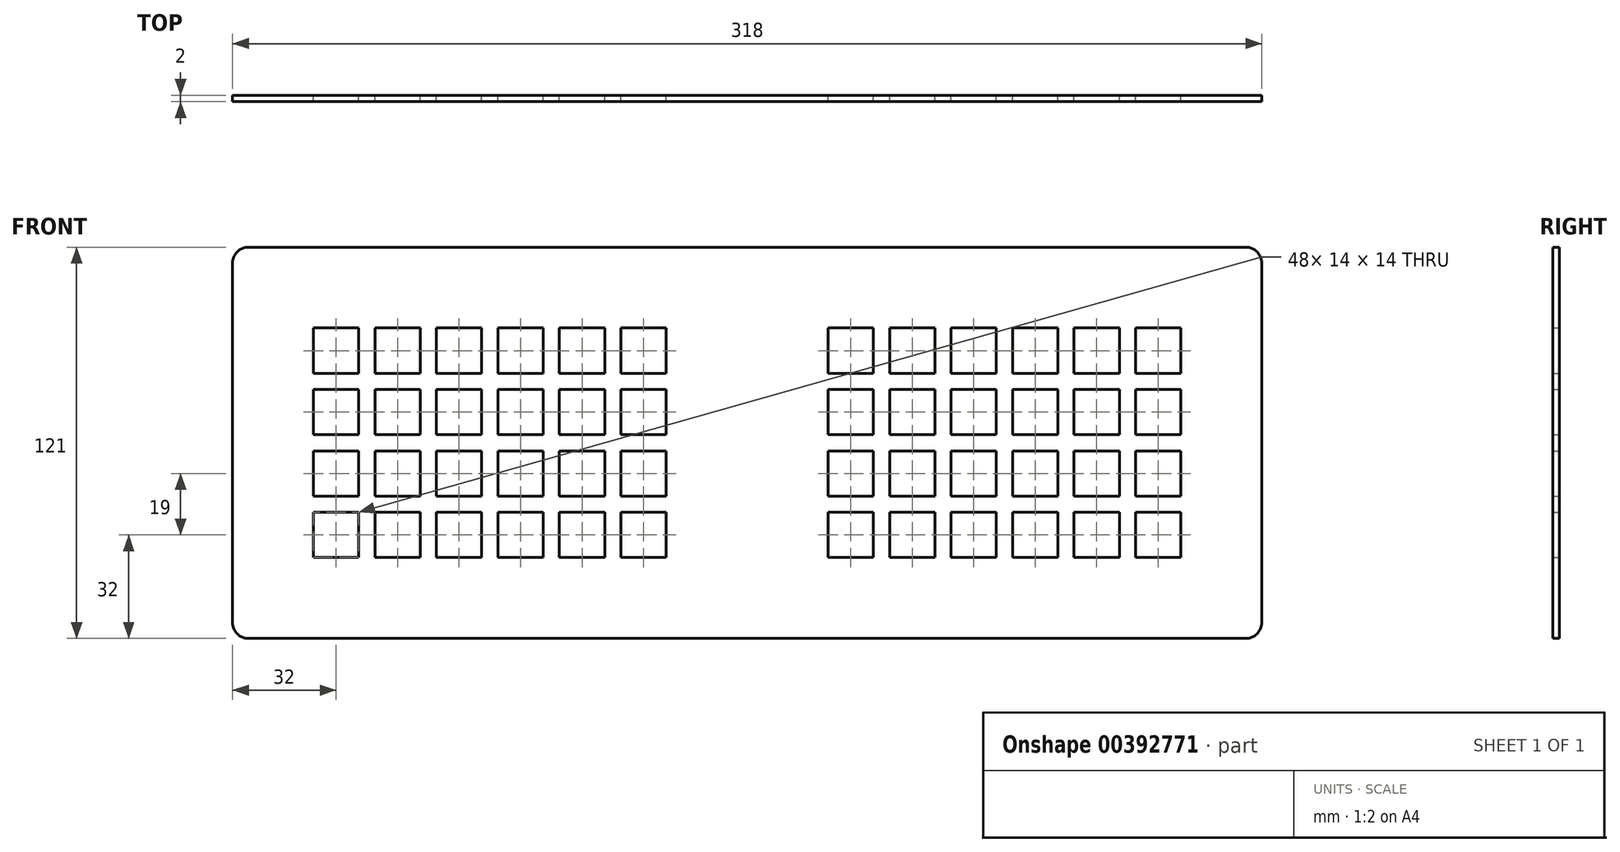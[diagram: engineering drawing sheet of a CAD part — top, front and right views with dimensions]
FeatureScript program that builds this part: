
annotation { "Feature Type Name" : "Feature", "Feature Type Description" : "" }
export const myFeature = defineFeature(function(context is Context, id is Id, definition is map)
    precondition{}
    {
        {
            var Q0;
            Q0=qCreatedBy(makeId("Front.planeOp"),FACE);
            var sketch = newSketch(context, id + "F0", { "sketchPlane" : qUnion([Q0])});
            skLineSegment(sketch, "E0.bottom", {"start": v(-120, 21.5) * mm, "end": v(-134, 21.5) * mm});
            skLineSegment(sketch, "E0.top", {"start": v(-120, 35.5) * mm, "end": v(-134, 35.5) * mm});
            skLineSegment(sketch, "E0.left", {"start": v(-120, 21.5) * mm, "end": v(-120, 35.5) * mm});
            skLineSegment(sketch, "E0.right", {"start": v(-134, 21.5) * mm, "end": v(-134, 35.5) * mm});
            skPoint(sketch, "E0.middle", {"position": v(-127, 28.5) * mm});
            skLineSegment(sketch, "E1.0.1.0", {"start": v(-120, 2.5) * mm, "end": v(-120, 16.5) * mm});
            skLineSegment(sketch, "E1.0.1.1", {"start": v(-134, 2.5) * mm, "end": v(-134, 16.5) * mm});
            skLineSegment(sketch, "E1.0.1.2", {"start": v(-120, 16.5) * mm, "end": v(-134, 16.5) * mm});
            skLineSegment(sketch, "E1.0.1.3", {"start": v(-120, 2.5) * mm, "end": v(-134, 2.5) * mm});
            skPoint(sketch, "E1.0.1.4", {"position": v(-127, 9.5) * mm});
            skLineSegment(sketch, "E1.0.2.0", {"start": v(-120, -16.5) * mm, "end": v(-120, -2.5) * mm});
            skLineSegment(sketch, "E1.0.2.1", {"start": v(-134, -16.5) * mm, "end": v(-134, -2.5) * mm});
            skLineSegment(sketch, "E1.0.2.2", {"start": v(-120, -2.5) * mm, "end": v(-134, -2.5) * mm});
            skLineSegment(sketch, "E1.0.2.3", {"start": v(-120, -16.5) * mm, "end": v(-134, -16.5) * mm});
            skPoint(sketch, "E1.0.2.4", {"position": v(-127, -9.5) * mm});
            skLineSegment(sketch, "E1.0.3.0", {"start": v(-120, -35.5) * mm, "end": v(-120, -21.5) * mm});
            skLineSegment(sketch, "E1.0.3.1", {"start": v(-134, -35.5) * mm, "end": v(-134, -21.5) * mm});
            skLineSegment(sketch, "E1.0.3.2", {"start": v(-120, -21.5) * mm, "end": v(-134, -21.5) * mm});
            skLineSegment(sketch, "E1.0.3.3", {"start": v(-120, -35.5) * mm, "end": v(-134, -35.5) * mm});
            skPoint(sketch, "E1.0.3.4", {"position": v(-127, -28.5) * mm});
            skLineSegment(sketch, "E1.1.0.0", {"start": v(-101, 21.5) * mm, "end": v(-101, 35.5) * mm});
            skLineSegment(sketch, "E1.1.0.1", {"start": v(-115, 21.5) * mm, "end": v(-115, 35.5) * mm});
            skLineSegment(sketch, "E1.1.0.2", {"start": v(-101, 35.5) * mm, "end": v(-115, 35.5) * mm});
            skLineSegment(sketch, "E1.1.0.3", {"start": v(-101, 21.5) * mm, "end": v(-115, 21.5) * mm});
            skPoint(sketch, "E1.1.0.4", {"position": v(-108, 28.5) * mm});
            skLineSegment(sketch, "E1.1.1.0", {"start": v(-101, 2.5) * mm, "end": v(-101, 16.5) * mm});
            skLineSegment(sketch, "E1.1.1.1", {"start": v(-115, 2.5) * mm, "end": v(-115, 16.5) * mm});
            skLineSegment(sketch, "E1.1.1.2", {"start": v(-101, 16.5) * mm, "end": v(-115, 16.5) * mm});
            skLineSegment(sketch, "E1.1.1.3", {"start": v(-101, 2.5) * mm, "end": v(-115, 2.5) * mm});
            skPoint(sketch, "E1.1.1.4", {"position": v(-108, 9.5) * mm});
            skLineSegment(sketch, "E1.1.2.0", {"start": v(-101, -16.5) * mm, "end": v(-101, -2.5) * mm});
            skLineSegment(sketch, "E1.1.2.1", {"start": v(-115, -16.5) * mm, "end": v(-115, -2.5) * mm});
            skLineSegment(sketch, "E1.1.2.2", {"start": v(-101, -2.5) * mm, "end": v(-115, -2.5) * mm});
            skLineSegment(sketch, "E1.1.2.3", {"start": v(-101, -16.5) * mm, "end": v(-115, -16.5) * mm});
            skPoint(sketch, "E1.1.2.4", {"position": v(-108, -9.5) * mm});
            skLineSegment(sketch, "E1.1.3.0", {"start": v(-101, -35.5) * mm, "end": v(-101, -21.5) * mm});
            skLineSegment(sketch, "E1.1.3.1", {"start": v(-115, -35.5) * mm, "end": v(-115, -21.5) * mm});
            skLineSegment(sketch, "E1.1.3.2", {"start": v(-101, -21.5) * mm, "end": v(-115, -21.5) * mm});
            skLineSegment(sketch, "E1.1.3.3", {"start": v(-101, -35.5) * mm, "end": v(-115, -35.5) * mm});
            skPoint(sketch, "E1.1.3.4", {"position": v(-108, -28.5) * mm});
            skLineSegment(sketch, "E1.2.0.0", {"start": v(-82, 21.5) * mm, "end": v(-82, 35.5) * mm});
            skLineSegment(sketch, "E1.2.0.1", {"start": v(-96, 21.5) * mm, "end": v(-96, 35.5) * mm});
            skLineSegment(sketch, "E1.2.0.2", {"start": v(-82, 35.5) * mm, "end": v(-96, 35.5) * mm});
            skLineSegment(sketch, "E1.2.0.3", {"start": v(-82, 21.5) * mm, "end": v(-96, 21.5) * mm});
            skPoint(sketch, "E1.2.0.4", {"position": v(-89, 28.5) * mm});
            skLineSegment(sketch, "E1.2.1.0", {"start": v(-82, 2.5) * mm, "end": v(-82, 16.5) * mm});
            skLineSegment(sketch, "E1.2.1.1", {"start": v(-96, 2.5) * mm, "end": v(-96, 16.5) * mm});
            skLineSegment(sketch, "E1.2.1.2", {"start": v(-82, 16.5) * mm, "end": v(-96, 16.5) * mm});
            skLineSegment(sketch, "E1.2.1.3", {"start": v(-82, 2.5) * mm, "end": v(-96, 2.5) * mm});
            skPoint(sketch, "E1.2.1.4", {"position": v(-89, 9.5) * mm});
            skLineSegment(sketch, "E1.2.2.0", {"start": v(-82, -16.5) * mm, "end": v(-82, -2.5) * mm});
            skLineSegment(sketch, "E1.2.2.1", {"start": v(-96, -16.5) * mm, "end": v(-96, -2.5) * mm});
            skLineSegment(sketch, "E1.2.2.2", {"start": v(-82, -2.5) * mm, "end": v(-96, -2.5) * mm});
            skLineSegment(sketch, "E1.2.2.3", {"start": v(-82, -16.5) * mm, "end": v(-96, -16.5) * mm});
            skPoint(sketch, "E1.2.2.4", {"position": v(-89, -9.5) * mm});
            skLineSegment(sketch, "E1.2.3.0", {"start": v(-82, -35.5) * mm, "end": v(-82, -21.5) * mm});
            skLineSegment(sketch, "E1.2.3.1", {"start": v(-96, -35.5) * mm, "end": v(-96, -21.5) * mm});
            skLineSegment(sketch, "E1.2.3.2", {"start": v(-82, -21.5) * mm, "end": v(-96, -21.5) * mm});
            skLineSegment(sketch, "E1.2.3.3", {"start": v(-82, -35.5) * mm, "end": v(-96, -35.5) * mm});
            skPoint(sketch, "E1.2.3.4", {"position": v(-89, -28.5) * mm});
            skLineSegment(sketch, "E1.3.0.0", {"start": v(-63, 21.5) * mm, "end": v(-63, 35.5) * mm});
            skLineSegment(sketch, "E1.3.0.1", {"start": v(-77, 21.5) * mm, "end": v(-77, 35.5) * mm});
            skLineSegment(sketch, "E1.3.0.2", {"start": v(-63, 35.5) * mm, "end": v(-77, 35.5) * mm});
            skLineSegment(sketch, "E1.3.0.3", {"start": v(-63, 21.5) * mm, "end": v(-77, 21.5) * mm});
            skPoint(sketch, "E1.3.0.4", {"position": v(-70, 28.5) * mm});
            skLineSegment(sketch, "E1.3.1.0", {"start": v(-63, 2.5) * mm, "end": v(-63, 16.5) * mm});
            skLineSegment(sketch, "E1.3.1.1", {"start": v(-77, 2.5) * mm, "end": v(-77, 16.5) * mm});
            skLineSegment(sketch, "E1.3.1.2", {"start": v(-63, 16.5) * mm, "end": v(-77, 16.5) * mm});
            skLineSegment(sketch, "E1.3.1.3", {"start": v(-63, 2.5) * mm, "end": v(-77, 2.5) * mm});
            skPoint(sketch, "E1.3.1.4", {"position": v(-70, 9.5) * mm});
            skLineSegment(sketch, "E1.3.2.0", {"start": v(-63, -16.5) * mm, "end": v(-63, -2.5) * mm});
            skLineSegment(sketch, "E1.3.2.1", {"start": v(-77, -16.5) * mm, "end": v(-77, -2.5) * mm});
            skLineSegment(sketch, "E1.3.2.2", {"start": v(-63, -2.5) * mm, "end": v(-77, -2.5) * mm});
            skLineSegment(sketch, "E1.3.2.3", {"start": v(-63, -16.5) * mm, "end": v(-77, -16.5) * mm});
            skPoint(sketch, "E1.3.2.4", {"position": v(-70, -9.5) * mm});
            skLineSegment(sketch, "E1.3.3.0", {"start": v(-63, -35.5) * mm, "end": v(-63, -21.5) * mm});
            skLineSegment(sketch, "E1.3.3.1", {"start": v(-77, -35.5) * mm, "end": v(-77, -21.5) * mm});
            skLineSegment(sketch, "E1.3.3.2", {"start": v(-63, -21.5) * mm, "end": v(-77, -21.5) * mm});
            skLineSegment(sketch, "E1.3.3.3", {"start": v(-63, -35.5) * mm, "end": v(-77, -35.5) * mm});
            skPoint(sketch, "E1.3.3.4", {"position": v(-70, -28.5) * mm});
            skLineSegment(sketch, "E1.4.0.0", {"start": v(-44, 21.5) * mm, "end": v(-44, 35.5) * mm});
            skLineSegment(sketch, "E1.4.0.1", {"start": v(-58, 21.5) * mm, "end": v(-58, 35.5) * mm});
            skLineSegment(sketch, "E1.4.0.2", {"start": v(-44, 35.5) * mm, "end": v(-58, 35.5) * mm});
            skLineSegment(sketch, "E1.4.0.3", {"start": v(-44, 21.5) * mm, "end": v(-58, 21.5) * mm});
            skPoint(sketch, "E1.4.0.4", {"position": v(-51, 28.5) * mm});
            skLineSegment(sketch, "E1.4.1.0", {"start": v(-44, 2.5) * mm, "end": v(-44, 16.5) * mm});
            skLineSegment(sketch, "E1.4.1.1", {"start": v(-58, 2.5) * mm, "end": v(-58, 16.5) * mm});
            skLineSegment(sketch, "E1.4.1.2", {"start": v(-44, 16.5) * mm, "end": v(-58, 16.5) * mm});
            skLineSegment(sketch, "E1.4.1.3", {"start": v(-44, 2.5) * mm, "end": v(-58, 2.5) * mm});
            skPoint(sketch, "E1.4.1.4", {"position": v(-51, 9.5) * mm});
            skLineSegment(sketch, "E1.4.2.0", {"start": v(-44, -16.5) * mm, "end": v(-44, -2.5) * mm});
            skLineSegment(sketch, "E1.4.2.1", {"start": v(-58, -16.5) * mm, "end": v(-58, -2.5) * mm});
            skLineSegment(sketch, "E1.4.2.2", {"start": v(-44, -2.5) * mm, "end": v(-58, -2.5) * mm});
            skLineSegment(sketch, "E1.4.2.3", {"start": v(-44, -16.5) * mm, "end": v(-58, -16.5) * mm});
            skPoint(sketch, "E1.4.2.4", {"position": v(-51, -9.5) * mm});
            skLineSegment(sketch, "E1.4.3.0", {"start": v(-44, -35.5) * mm, "end": v(-44, -21.5) * mm});
            skLineSegment(sketch, "E1.4.3.1", {"start": v(-58, -35.5) * mm, "end": v(-58, -21.5) * mm});
            skLineSegment(sketch, "E1.4.3.2", {"start": v(-44, -21.5) * mm, "end": v(-58, -21.5) * mm});
            skLineSegment(sketch, "E1.4.3.3", {"start": v(-44, -35.5) * mm, "end": v(-58, -35.5) * mm});
            skPoint(sketch, "E1.4.3.4", {"position": v(-51, -28.5) * mm});
            skLineSegment(sketch, "E1.5.0.0", {"start": v(-25, 21.5) * mm, "end": v(-25, 35.5) * mm});
            skLineSegment(sketch, "E1.5.0.1", {"start": v(-39, 21.5) * mm, "end": v(-39, 35.5) * mm});
            skLineSegment(sketch, "E1.5.0.2", {"start": v(-25, 35.5) * mm, "end": v(-39, 35.5) * mm});
            skLineSegment(sketch, "E1.5.0.3", {"start": v(-25, 21.5) * mm, "end": v(-39, 21.5) * mm});
            skPoint(sketch, "E1.5.0.4", {"position": v(-32, 28.5) * mm});
            skLineSegment(sketch, "E1.5.1.0", {"start": v(-25, 2.5) * mm, "end": v(-25, 16.5) * mm});
            skLineSegment(sketch, "E1.5.1.1", {"start": v(-39, 2.5) * mm, "end": v(-39, 16.5) * mm});
            skLineSegment(sketch, "E1.5.1.2", {"start": v(-25, 16.5) * mm, "end": v(-39, 16.5) * mm});
            skLineSegment(sketch, "E1.5.1.3", {"start": v(-25, 2.5) * mm, "end": v(-39, 2.5) * mm});
            skPoint(sketch, "E1.5.1.4", {"position": v(-32, 9.5) * mm});
            skLineSegment(sketch, "E1.5.2.0", {"start": v(-25, -16.5) * mm, "end": v(-25, -2.5) * mm});
            skLineSegment(sketch, "E1.5.2.1", {"start": v(-39, -16.5) * mm, "end": v(-39, -2.5) * mm});
            skLineSegment(sketch, "E1.5.2.2", {"start": v(-25, -2.5) * mm, "end": v(-39, -2.5) * mm});
            skLineSegment(sketch, "E1.5.2.3", {"start": v(-25, -16.5) * mm, "end": v(-39, -16.5) * mm});
            skPoint(sketch, "E1.5.2.4", {"position": v(-32, -9.5) * mm});
            skLineSegment(sketch, "E1.5.3.0", {"start": v(-25, -35.5) * mm, "end": v(-25, -21.5) * mm});
            skLineSegment(sketch, "E1.5.3.1", {"start": v(-39, -35.5) * mm, "end": v(-39, -21.5) * mm});
            skLineSegment(sketch, "E1.5.3.2", {"start": v(-25, -21.5) * mm, "end": v(-39, -21.5) * mm});
            skLineSegment(sketch, "E1.5.3.3", {"start": v(-25, -35.5) * mm, "end": v(-39, -35.5) * mm});
            skPoint(sketch, "E1.5.3.4", {"position": v(-32, -28.5) * mm});
            skLineSegment(sketch, "E1.direction1", {"start": v(-120, 21.5) * mm, "end": v(-101, 21.5) * mm, "construction": true});
            skLineSegment(sketch, "E1.direction2", {"start": v(-120, 21.5) * mm, "end": v(-120, 2.5) * mm, "construction": true});
            skPoint(sketch, "E2.1.0.0", {"position": v(89, -28.5) * mm});
            skLineSegment(sketch, "E2.1.0.1", {"start": v(96, -2.5) * mm, "end": v(82, -2.5) * mm});
            skLineSegment(sketch, "E2.1.0.2", {"start": v(77, -2.5) * mm, "end": v(63, -2.5) * mm});
            skLineSegment(sketch, "E2.1.0.3", {"start": v(58, -2.5) * mm, "end": v(44, -2.5) * mm});
            skLineSegment(sketch, "E2.1.0.4", {"start": v(134, -2.5) * mm, "end": v(120, -2.5) * mm});
            skLineSegment(sketch, "E2.1.0.5", {"start": v(115, -2.5) * mm, "end": v(101, -2.5) * mm});
            skLineSegment(sketch, "E2.1.0.6", {"start": v(134, 21.5) * mm, "end": v(120, 21.5) * mm});
            skLineSegment(sketch, "E2.1.0.7", {"start": v(115, 21.5) * mm, "end": v(101, 21.5) * mm});
            skLineSegment(sketch, "E2.1.0.8", {"start": v(96, 21.5) * mm, "end": v(82, 21.5) * mm});
            skLineSegment(sketch, "E2.1.0.9", {"start": v(77, 21.5) * mm, "end": v(63, 21.5) * mm});
            skPoint(sketch, "E2.1.0.10", {"position": v(127, -9.5) * mm});
            skPoint(sketch, "E2.1.0.11", {"position": v(51, -9.5) * mm});
            skPoint(sketch, "E2.1.0.12", {"position": v(32, 28.5) * mm});
            skPoint(sketch, "E2.1.0.13", {"position": v(108, 28.5) * mm});
            skPoint(sketch, "E2.1.0.14", {"position": v(70, 9.5) * mm});
            skLineSegment(sketch, "E2.1.0.15", {"start": v(96, -16.5) * mm, "end": v(82, -16.5) * mm});
            skLineSegment(sketch, "E2.1.0.16", {"start": v(77, -16.5) * mm, "end": v(63, -16.5) * mm});
            skLineSegment(sketch, "E2.1.0.17", {"start": v(58, -16.5) * mm, "end": v(44, -16.5) * mm});
            skLineSegment(sketch, "E2.1.0.18", {"start": v(134, -16.5) * mm, "end": v(120, -16.5) * mm});
            skLineSegment(sketch, "E2.1.0.19", {"start": v(115, -16.5) * mm, "end": v(101, -16.5) * mm});
            skLineSegment(sketch, "E2.1.0.20", {"start": v(58, 2.5) * mm, "end": v(58, 16.5) * mm});
            skLineSegment(sketch, "E2.1.0.21", {"start": v(101, -35.5) * mm, "end": v(101, -21.5) * mm});
            skLineSegment(sketch, "E2.1.0.22", {"start": v(134, 2.5) * mm, "end": v(134, 16.5) * mm});
            skLineSegment(sketch, "E2.1.0.23", {"start": v(115, 2.5) * mm, "end": v(115, 16.5) * mm});
            skLineSegment(sketch, "E2.1.0.24", {"start": v(82, -35.5) * mm, "end": v(82, -21.5) * mm});
            skLineSegment(sketch, "E2.1.0.25", {"start": v(96, 2.5) * mm, "end": v(96, 16.5) * mm});
            skLineSegment(sketch, "E2.1.0.26", {"start": v(63, -35.5) * mm, "end": v(63, -21.5) * mm});
            skLineSegment(sketch, "E2.1.0.27", {"start": v(77, 2.5) * mm, "end": v(77, 16.5) * mm});
            skLineSegment(sketch, "E2.1.0.28", {"start": v(44, -35.5) * mm, "end": v(44, -21.5) * mm});
            skLineSegment(sketch, "E2.1.0.29", {"start": v(120, -35.5) * mm, "end": v(120, -21.5) * mm});
            skPoint(sketch, "E2.1.0.30", {"position": v(127, -28.5) * mm});
            skPoint(sketch, "E2.1.0.31", {"position": v(51, -28.5) * mm});
            skPoint(sketch, "E2.1.0.32", {"position": v(32, 9.5) * mm});
            skPoint(sketch, "E2.1.0.33", {"position": v(70, -9.5) * mm});
            skPoint(sketch, "E2.1.0.34", {"position": v(108, 9.5) * mm});
            skLineSegment(sketch, "E2.1.0.35", {"start": v(96, -35.5) * mm, "end": v(96, -21.5) * mm});
            skLineSegment(sketch, "E2.1.0.36", {"start": v(77, -35.5) * mm, "end": v(77, -21.5) * mm});
            skLineSegment(sketch, "E2.1.0.37", {"start": v(58, -35.5) * mm, "end": v(58, -21.5) * mm});
            skLineSegment(sketch, "E2.1.0.38", {"start": v(134, -35.5) * mm, "end": v(134, -21.5) * mm});
            skLineSegment(sketch, "E2.1.0.39", {"start": v(115, -35.5) * mm, "end": v(115, -21.5) * mm});
            skLineSegment(sketch, "E2.1.0.40", {"start": v(44, 2.5) * mm, "end": v(44, 16.5) * mm});
            skLineSegment(sketch, "E2.1.0.41", {"start": v(115, -21.5) * mm, "end": v(101, -21.5) * mm});
            skLineSegment(sketch, "E2.1.0.42", {"start": v(120, 2.5) * mm, "end": v(120, 16.5) * mm});
            skLineSegment(sketch, "E2.1.0.43", {"start": v(101, 2.5) * mm, "end": v(101, 16.5) * mm});
            skLineSegment(sketch, "E2.1.0.44", {"start": v(96, -21.5) * mm, "end": v(82, -21.5) * mm});
            skLineSegment(sketch, "E2.1.0.45", {"start": v(77, -21.5) * mm, "end": v(63, -21.5) * mm});
            skLineSegment(sketch, "E2.1.0.46", {"start": v(82, 2.5) * mm, "end": v(82, 16.5) * mm});
            skLineSegment(sketch, "E2.1.0.47", {"start": v(63, 2.5) * mm, "end": v(63, 16.5) * mm});
            skLineSegment(sketch, "E2.1.0.48", {"start": v(58, -21.5) * mm, "end": v(44, -21.5) * mm});
            skLineSegment(sketch, "E2.1.0.49", {"start": v(134, -21.5) * mm, "end": v(120, -21.5) * mm});
            skPoint(sketch, "E2.1.0.50", {"position": v(70, 28.5) * mm});
            skPoint(sketch, "E2.1.0.51", {"position": v(32, -9.5) * mm});
            skPoint(sketch, "E2.1.0.52", {"position": v(108, -9.5) * mm});
            skPoint(sketch, "E2.1.0.53", {"position": v(70, -28.5) * mm});
            skLineSegment(sketch, "E2.1.0.54", {"start": v(58, 16.5) * mm, "end": v(44, 16.5) * mm});
            skLineSegment(sketch, "E2.1.0.55", {"start": v(115, -35.5) * mm, "end": v(101, -35.5) * mm});
            skLineSegment(sketch, "E2.1.0.56", {"start": v(134, 16.5) * mm, "end": v(120, 16.5) * mm});
            skLineSegment(sketch, "E2.1.0.57", {"start": v(96, -35.5) * mm, "end": v(82, -35.5) * mm});
            skLineSegment(sketch, "E2.1.0.58", {"start": v(115, 16.5) * mm, "end": v(101, 16.5) * mm});
            skLineSegment(sketch, "E2.1.0.59", {"start": v(77, -35.5) * mm, "end": v(63, -35.5) * mm});
            skLineSegment(sketch, "E2.1.0.60", {"start": v(96, 16.5) * mm, "end": v(82, 16.5) * mm});
            skLineSegment(sketch, "E2.1.0.61", {"start": v(77, 16.5) * mm, "end": v(63, 16.5) * mm});
            skLineSegment(sketch, "E2.1.0.62", {"start": v(58, -35.5) * mm, "end": v(44, -35.5) * mm});
            skLineSegment(sketch, "E2.1.0.63", {"start": v(134, -35.5) * mm, "end": v(120, -35.5) * mm});
            skLineSegment(sketch, "E2.1.0.64", {"start": v(25, -35.5) * mm, "end": v(25, -21.5) * mm});
            skLineSegment(sketch, "E2.1.0.65", {"start": v(39, -21.5) * mm, "end": v(25, -21.5) * mm});
            skLineSegment(sketch, "E2.1.0.66", {"start": v(39, -35.5) * mm, "end": v(25, -35.5) * mm});
            skLineSegment(sketch, "E2.1.0.67", {"start": v(39, 21.5) * mm, "end": v(25, 21.5) * mm});
            skLineSegment(sketch, "E2.1.0.68", {"start": v(39, 35.5) * mm, "end": v(25, 35.5) * mm});
            skLineSegment(sketch, "E2.1.0.69", {"start": v(39, 21.5) * mm, "end": v(39, 35.5) * mm});
            skLineSegment(sketch, "E2.1.0.70", {"start": v(25, 21.5) * mm, "end": v(25, 35.5) * mm});
            skLineSegment(sketch, "E2.1.0.71", {"start": v(25, 2.5) * mm, "end": v(25, 16.5) * mm});
            skLineSegment(sketch, "E2.1.0.72", {"start": v(39, 16.5) * mm, "end": v(25, 16.5) * mm});
            skLineSegment(sketch, "E2.1.0.73", {"start": v(39, 2.5) * mm, "end": v(25, 2.5) * mm});
            skLineSegment(sketch, "E2.1.0.74", {"start": v(39, -16.5) * mm, "end": v(39, -2.5) * mm});
            skLineSegment(sketch, "E2.1.0.75", {"start": v(25, -16.5) * mm, "end": v(25, -2.5) * mm});
            skLineSegment(sketch, "E2.1.0.76", {"start": v(39, -2.5) * mm, "end": v(25, -2.5) * mm});
            skLineSegment(sketch, "E2.1.0.77", {"start": v(39, -16.5) * mm, "end": v(25, -16.5) * mm});
            skLineSegment(sketch, "E2.1.0.78", {"start": v(39, -35.5) * mm, "end": v(39, -21.5) * mm});
            skLineSegment(sketch, "E2.1.0.79", {"start": v(39, 21.5) * mm, "end": v(58, 21.5) * mm, "construction": true});
            skPoint(sketch, "E2.1.0.80", {"position": v(108, -28.5) * mm});
            skPoint(sketch, "E2.1.0.81", {"position": v(32, -28.5) * mm});
            skLineSegment(sketch, "E2.1.0.82", {"start": v(96, 2.5) * mm, "end": v(82, 2.5) * mm});
            skLineSegment(sketch, "E2.1.0.83", {"start": v(77, 2.5) * mm, "end": v(63, 2.5) * mm});
            skLineSegment(sketch, "E2.1.0.84", {"start": v(58, 2.5) * mm, "end": v(44, 2.5) * mm});
            skLineSegment(sketch, "E2.1.0.85", {"start": v(134, 2.5) * mm, "end": v(120, 2.5) * mm});
            skLineSegment(sketch, "E2.1.0.86", {"start": v(115, 2.5) * mm, "end": v(101, 2.5) * mm});
            skPoint(sketch, "E2.1.0.87", {"position": v(89, 28.5) * mm});
            skLineSegment(sketch, "E2.1.0.88", {"start": v(58, 21.5) * mm, "end": v(58, 35.5) * mm});
            skLineSegment(sketch, "E2.1.0.89", {"start": v(134, 21.5) * mm, "end": v(134, 35.5) * mm});
            skLineSegment(sketch, "E2.1.0.90", {"start": v(115, 21.5) * mm, "end": v(115, 35.5) * mm});
            skLineSegment(sketch, "E2.1.0.91", {"start": v(96, 21.5) * mm, "end": v(96, 35.5) * mm});
            skLineSegment(sketch, "E2.1.0.92", {"start": v(77, 21.5) * mm, "end": v(77, 35.5) * mm});
            skPoint(sketch, "E2.1.0.93", {"position": v(127, 28.5) * mm});
            skPoint(sketch, "E2.1.0.94", {"position": v(51, 28.5) * mm});
            skLineSegment(sketch, "E2.1.0.95", {"start": v(96, -16.5) * mm, "end": v(96, -2.5) * mm});
            skLineSegment(sketch, "E2.1.0.96", {"start": v(77, -16.5) * mm, "end": v(77, -2.5) * mm});
            skLineSegment(sketch, "E2.1.0.97", {"start": v(58, -16.5) * mm, "end": v(58, -2.5) * mm});
            skLineSegment(sketch, "E2.1.0.98", {"start": v(134, -16.5) * mm, "end": v(134, -2.5) * mm});
            skLineSegment(sketch, "E2.1.0.99", {"start": v(115, -16.5) * mm, "end": v(115, -2.5) * mm});
            skPoint(sketch, "E2.1.0.100", {"position": v(89, 9.5) * mm});
            skLineSegment(sketch, "E2.1.0.101", {"start": v(44, 21.5) * mm, "end": v(44, 35.5) * mm});
            skLineSegment(sketch, "E2.1.0.102", {"start": v(120, 21.5) * mm, "end": v(120, 35.5) * mm});
            skLineSegment(sketch, "E2.1.0.103", {"start": v(101, 21.5) * mm, "end": v(101, 35.5) * mm});
            skLineSegment(sketch, "E2.1.0.104", {"start": v(82, 21.5) * mm, "end": v(82, 35.5) * mm});
            skLineSegment(sketch, "E2.1.0.105", {"start": v(63, 21.5) * mm, "end": v(63, 35.5) * mm});
            skLineSegment(sketch, "E2.1.0.106", {"start": v(39, 21.5) * mm, "end": v(39, 2.5) * mm, "construction": true});
            skLineSegment(sketch, "E2.1.0.107", {"start": v(82, -16.5) * mm, "end": v(82, -2.5) * mm});
            skLineSegment(sketch, "E2.1.0.108", {"start": v(63, -16.5) * mm, "end": v(63, -2.5) * mm});
            skLineSegment(sketch, "E2.1.0.109", {"start": v(44, -16.5) * mm, "end": v(44, -2.5) * mm});
            skLineSegment(sketch, "E2.1.0.110", {"start": v(120, -16.5) * mm, "end": v(120, -2.5) * mm});
            skLineSegment(sketch, "E2.1.0.111", {"start": v(101, -16.5) * mm, "end": v(101, -2.5) * mm});
            skPoint(sketch, "E2.1.0.112", {"position": v(89, -9.5) * mm});
            skLineSegment(sketch, "E2.1.0.113", {"start": v(58, 35.5) * mm, "end": v(44, 35.5) * mm});
            skLineSegment(sketch, "E2.1.0.114", {"start": v(134, 35.5) * mm, "end": v(120, 35.5) * mm});
            skLineSegment(sketch, "E2.1.0.115", {"start": v(115, 35.5) * mm, "end": v(101, 35.5) * mm});
            skLineSegment(sketch, "E2.1.0.116", {"start": v(96, 35.5) * mm, "end": v(82, 35.5) * mm});
            skLineSegment(sketch, "E2.1.0.117", {"start": v(77, 35.5) * mm, "end": v(63, 35.5) * mm});
            skPoint(sketch, "E2.1.0.118", {"position": v(127, 9.5) * mm});
            skPoint(sketch, "E2.1.0.119", {"position": v(51, 9.5) * mm});
            skLineSegment(sketch, "E2.1.0.120", {"start": v(58, 21.5) * mm, "end": v(44, 21.5) * mm});
            skLineSegment(sketch, "E2.1.0.121", {"start": v(39, 2.5) * mm, "end": v(39, 16.5) * mm});
            skLineSegment(sketch, "E2.direction1", {"start": v(-134, -35.5) * mm, "end": v(25, -35.5) * mm, "construction": true});
            skPoint(sketch, "E3", {"position": v(0, 0) * mm});
            skLineSegment(sketch, "E4", {"start": v(-25, -2.5) * mm, "end": v(25, 2.5) * mm, "construction": true});
            skLineSegment(sketch, "E5.bottom", {"start": v(-154, 60.5) * mm, "end": v(154, 60.5) * mm});
            skLineSegment(sketch, "E5.top", {"start": v(-154, -60.5) * mm, "end": v(154, -60.5) * mm});
            skLineSegment(sketch, "E5.left", {"start": v(-159, 55.5) * mm, "end": v(-159, -55.5) * mm});
            skLineSegment(sketch, "E5.right", {"start": v(159, 55.5) * mm, "end": v(159, -55.5) * mm});
            skPoint(sketch, "E6.visualSharp", {"position": v(-159, 60.5) * mm});
            skArc(sketch, "E6.filletArc", {"start": v(-154, 60.5) * mm, "mid": v(-157.54, 59.04) * mm, "end": v(-159, 55.5) * mm});
            skPoint(sketch, "E7.visualSharp", {"position": v(159, 60.5) * mm});
            skArc(sketch, "E7.filletArc", {"start": v(159, 55.5) * mm, "mid": v(157.54, 59.04) * mm, "end": v(154, 60.5) * mm});
            skPoint(sketch, "E8.visualSharp", {"position": v(159, -60.5) * mm});
            skArc(sketch, "E8.filletArc", {"start": v(154, -60.5) * mm, "mid": v(157.54, -59.04) * mm, "end": v(159, -55.5) * mm});
            skPoint(sketch, "E9.visualSharp", {"position": v(-159, -60.5) * mm});
            skArc(sketch, "E9.filletArc", {"start": v(-159, -55.5) * mm, "mid": v(-157.54, -59.04) * mm, "end": v(-154, -60.5) * mm});
            skSolve(sketch);
        }
        {
            var Q0;
            Q0 = qSketchRegion(id + "F0", true);
            extrude(context, id + "F1", {"entities" : qUnion([Q0]), "depth" : 2 * mm});
        }
    });
